# Revit family: 50918191
name_source: partatom
category: Plumbing Fixtures
revit_build: Autodesk Revit 2016 (Build: 20150220_1215(x64)
units: mm (PartAtom-declared; Revit-internal decimal feet)

## family parameters
Always vertical = Yes
Cut with Voids When Loaded = No
OmniClass Number = 23.45.55.00
OmniClass Title = Sanitary Faucets, Wastes
Part Type = Normal
Room Calculation Point = No
Round Connector Dimension = Use Diameter
Shared = No
Work Plane-Based = No

## types (1)
- 50918191 Washbasin faucet
    2D/3D/BIM Files URL = http://static.hansa.com
    Advanced Features = DZR brass;Twist-resistant
    Aerator = CACHÉ® integrated aerator
    Approval ACS = 16 ACC LY 700
    AssetType = Fixed
    BIMObjectName = 50918191
    BodyMaterial = Brass
    Brand = Hansa
    Catalog Drawing URL = http://static.hansa.com
    Category = Bathroom;Public & Semi-public
    Class = Single lever
    CloseOffRating = 0
    Color = Chrome
    Connection = Cold water connection
    Connection Size = G1/2
    ConvergoRefNr = 0087-1803-0046-FI
    Customs Code = 84818011
    DN Size = DN15
    DurationUnit = Year
    EAN Number = 4015474171756
    Extensions = No pop-up waste included
    FDV Document URL = http://www.hansa.com
    FaucetMainMaterial = Brass
    Features = Single lever
    Finish = Polished
    Flow Drawing URL = http://static.hansa.com
    Flow Rate At 300kPa = 0.1 L/s
    FlowCoefficient = 0
    Group = Washbasin faucets
    IfcExportAs = IfcValveType
    IfcExportType = FAUCET
    InletConnectionSize = 15 mm  [stored 0.0492126 ft]
    Installation Type = Deck mounted
    Installation and Maintenance = http://static.hansa.com
    ManufacterURL = http://www.hansa.com
    Manufacturer = Hansa
    ManufacturerName = Hansa
    Market = AUT;BEL;CZE;DEU;ESP;FRA;INT;ITA;NLD;SVK
    Material = Brass
    Mechanical Parts = Ceramic head part
    Model = 50918191 Washbasin faucet
    ModelReference = 50918191
    Mounting Holes = 1 mounting hole
    NBSDescription = Water supply fittings for wash basins and troughs
    NBSReference = 45-35-70/371
    Name = 50918191 Washbasin faucet
    Name_en = 50918191 Washbasin faucet
    NominalDepth = 167 mm
    NominalHeight = 244 mm  [stored 0.800525 ft]
    NominalWidth = 53 mm  [stored 0.173885 ft]
    OutletConnectionSize = 15 mm  [stored 0.0492126 ft]
    Package Weight = 1.80 kg
    Package external Dimensions = 283 x 271 x 55
    Pipes = Flexible inlet pipe(s)
    Product Code = 50918191
    Product Datasheet = http://www.hansa.com
    Product Family = HANSANOVA Style
    Product Image URL = http://static.hansa.com
    Product URL = http://static.hansa.com
    Projection = 131 mm
    Revision = 2
    Shape = Sculptured
    Size = 53x167x244 mm
    Spout Type = Fixed spout
    URL ACS = http://static.hansa.com
    Uniclass2 = Pr_40_30_96_99
    Uniclass2015Description = Washbasin thermostatic water supply sets
    Uniclass2015Reference = Pr_40_20_87_99
    Version = 2
    VersionDate = 01/01/2019
    WarrantyDescription = http://warranty.hansa.com
    WarrantyDurationUnit = Year

note: [stored X ft] marks values corroborated as IEEE doubles in the binary element streams (Revit-internal decimal feet)

## geometry (parser evidence)
native form markers: Sweep x3
no freeform markers — native parametric forms only
